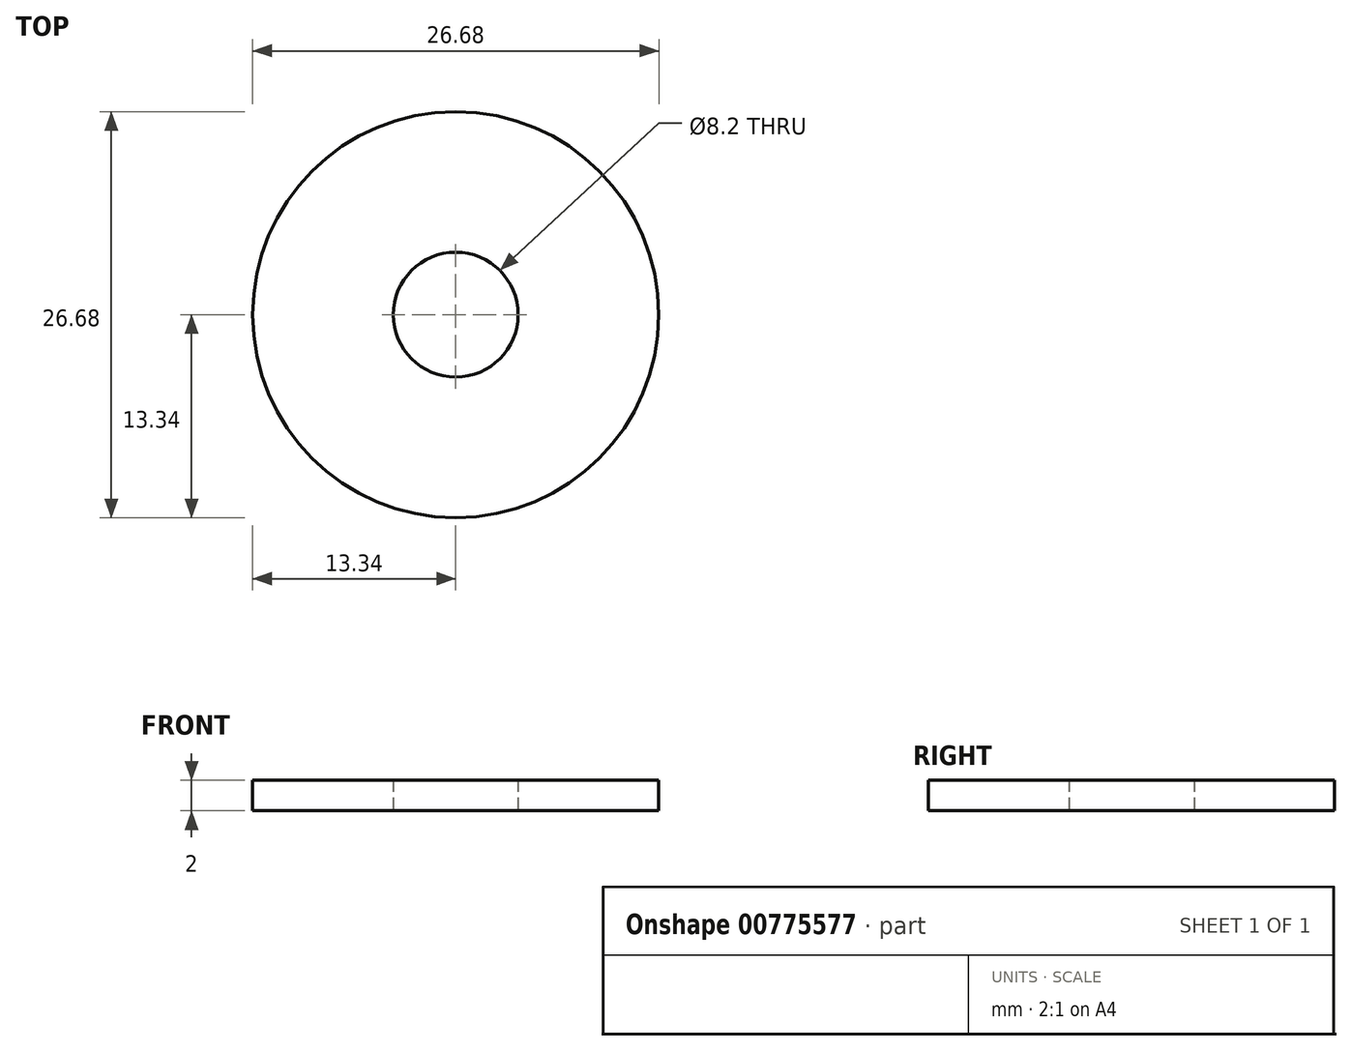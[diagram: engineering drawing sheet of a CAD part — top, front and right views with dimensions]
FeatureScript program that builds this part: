
annotation { "Feature Type Name" : "Feature", "Feature Type Description" : "" }
export const myFeature = defineFeature(function(context is Context, id is Id, definition is map)
    precondition{}
    {
        {
            var Q0;
            Q0=qCreatedBy(makeId("Top.planeOp"),FACE);
            var sketch = newSketch(context, id + "F0", { "sketchPlane" : qUnion([Q0])});
            skCircle(sketch, "E0", {"center": v(0, 0) * mm, "radius": 13.34 * mm});
            skCircle(sketch, "E1", {"center": v(0, 0) * mm, "radius": 4.1 * mm});
            skSolve(sketch);
        }
        {
            var Q0;
            Q0 = qSketchRegion(id + "F0", true);
            extrude(context, id + "F1", {"entities" : qUnion([Q0]), "depth" : 2 * mm, "offsetDistance" : 25.4 * mm});
        }
    });
